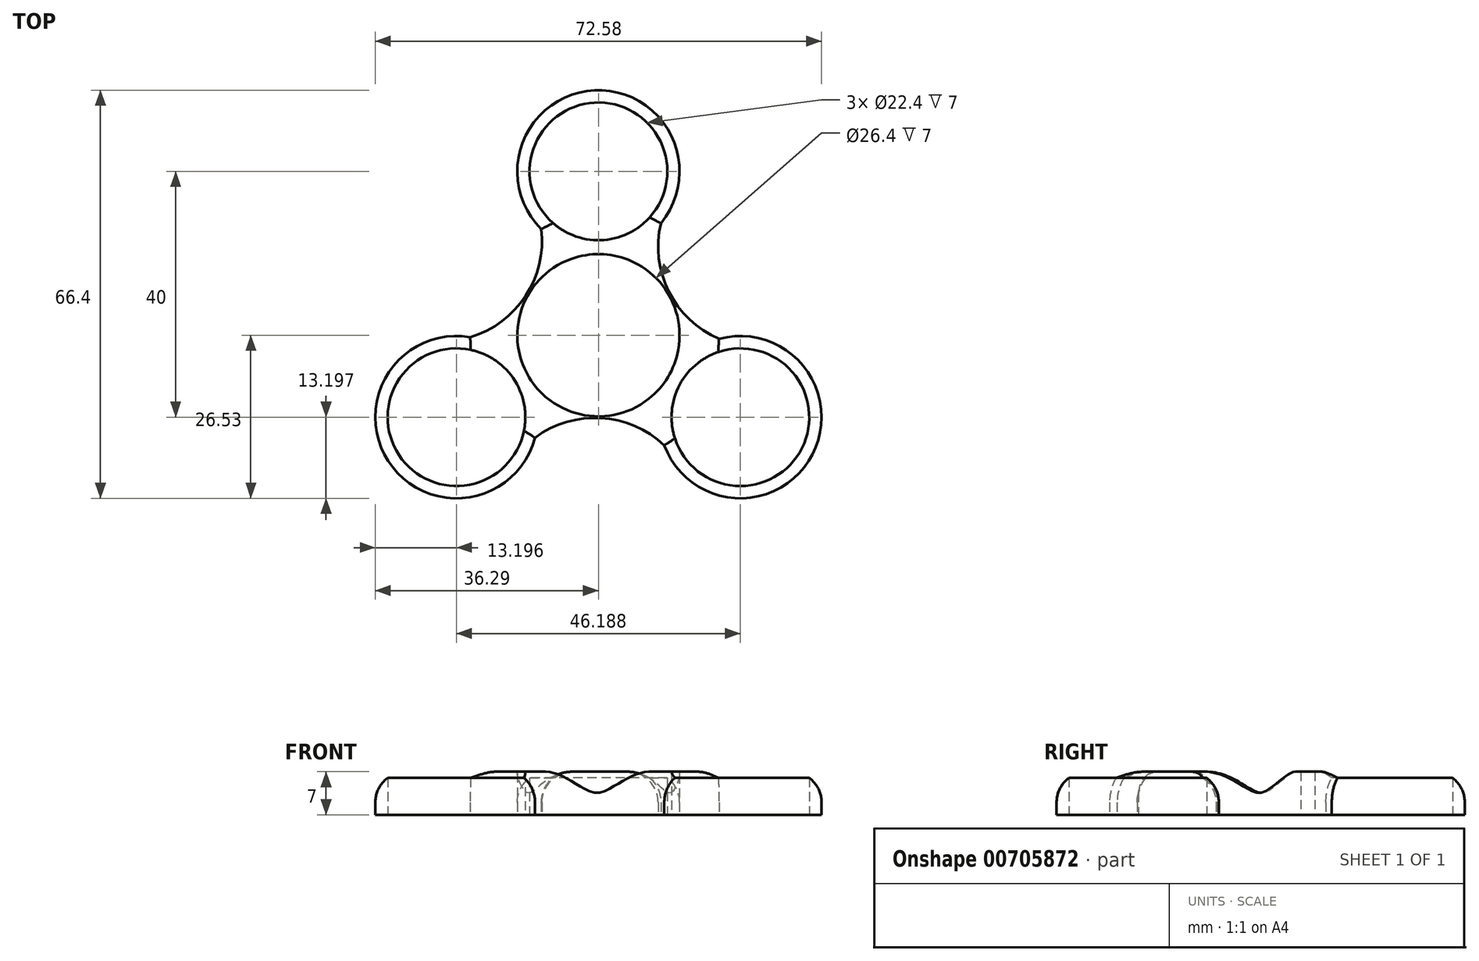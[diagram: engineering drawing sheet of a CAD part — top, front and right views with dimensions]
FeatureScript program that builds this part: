
annotation { "Feature Type Name" : "Feature", "Feature Type Description" : "" }
export const myFeature = defineFeature(function(context is Context, id is Id, definition is map)
    precondition{}
    {
        {
            var Q0;
            Q0=qCreatedBy(makeId("Top.planeOp"),FACE);
            var sketch = newSketch(context, id + "F0", { "sketchPlane" : qUnion([Q0])});
            skCircle(sketch, "E0", {"center": v(0, 0) * mm, "radius": 11.2 * mm});
            skCircle(sketch, "E1", {"center": v(0, 0) * mm, "radius": 13.2 * mm});
            skCircle(sketch, "E2", {"center": v(0, 26.67) * mm, "radius": 11.2 * mm});
            skArc(sketch, "E3", {"start": v(10.16, 18.23) * mm, "mid": v(-0.64, 39.85) * mm, "end": v(-9.28, 17.28) * mm});
            skArc(sketch, "E4.1.0", {"start": v(-20.87, -0.32) * mm, "mid": v(-34.19, -20.48) * mm, "end": v(-10.33, -16.68) * mm});
            skCircle(sketch, "E4.1.1", {"center": v(-23.1, -13.33) * mm, "radius": 11.2 * mm});
            skArc(sketch, "E4.2.0", {"start": v(10.71, -17.91) * mm, "mid": v(34.83, -19.37) * mm, "end": v(19.61, -0.6) * mm});
            skCircle(sketch, "E4.2.1", {"center": v(23.1, -13.33) * mm, "radius": 11.2 * mm});
            skArc(sketch, "E5", {"start": v(10.16, 18.23) * mm, "mid": v(11.45, 7.1) * mm, "end": v(19.61, -0.6) * mm});
            skArc(sketch, "E6.1.0", {"start": v(-20.87, -0.32) * mm, "mid": v(-11.87, 6.37) * mm, "end": v(-9.28, 17.28) * mm});
            skArc(sketch, "E6.2.0", {"start": v(10.71, -17.91) * mm, "mid": v(0.42, -13.47) * mm, "end": v(-10.33, -16.68) * mm});
            skSolve(sketch);
        }
        {
            var Q0;
            Q0=makeQuery(id+"F0.imprint","IMPRINT",FACE,{"disambiguationData":[TD([[makeQuery(id+"F0.imprint","IMPRINT",EDGE,{"derivedFrom":sQuery(id+"F0.wireOp",EDGE,"E1")}),-1.0]])]});
            extrude(context, id + "F1", {"entities" : qUnion([Q0]), "depth" : 7 * mm, "offsetDistance" : 25 * mm});
        }
        {
            var Q0;
            Q0=makeQuery(id+"F1.opExtrude","CAP_EDGE",EDGE,{"disambiguationData":[OSD([sQuery(id+"F0.wireOp",EDGE,"E6.1.0")])],"isStart":false});
            var Q1;
            Q1=makeQuery(id+"F1.opExtrude","CAP_EDGE",EDGE,{"disambiguationData":[OSD([sQuery(id+"F0.wireOp",EDGE,"E4.1.0")])],"isStart":false});
            var Q2;
            Q2=makeQuery(id+"F1.opExtrude","CAP_EDGE",EDGE,{"disambiguationData":[OSD([sQuery(id+"F0.wireOp",EDGE,"E6.2.0")])],"isStart":false});
            var Q3;
            Q3=makeQuery(id+"F1.opExtrude","CAP_EDGE",EDGE,{"disambiguationData":[OSD([sQuery(id+"F0.wireOp",EDGE,"E4.2.0")])],"isStart":false});
            var Q4;
            Q4=makeQuery(id+"F1.opExtrude","CAP_EDGE",EDGE,{"disambiguationData":[OSD([sQuery(id+"F0.wireOp",EDGE,"E5")])],"isStart":false});
            var Q5;
            Q5=makeQuery(id+"F1.opExtrude","CAP_EDGE",EDGE,{"disambiguationData":[OSD([sQuery(id+"F0.wireOp",EDGE,"E3")])],"isStart":false});
            fillet(context, id + "F2", {"entities" : qUnion([Q0, Q1, Q2, Q3, Q4, Q5]), "radius" : 5 * mm, "tangentPropagation" : true, "allowEdgeOverflow" : false});
        }
    });
